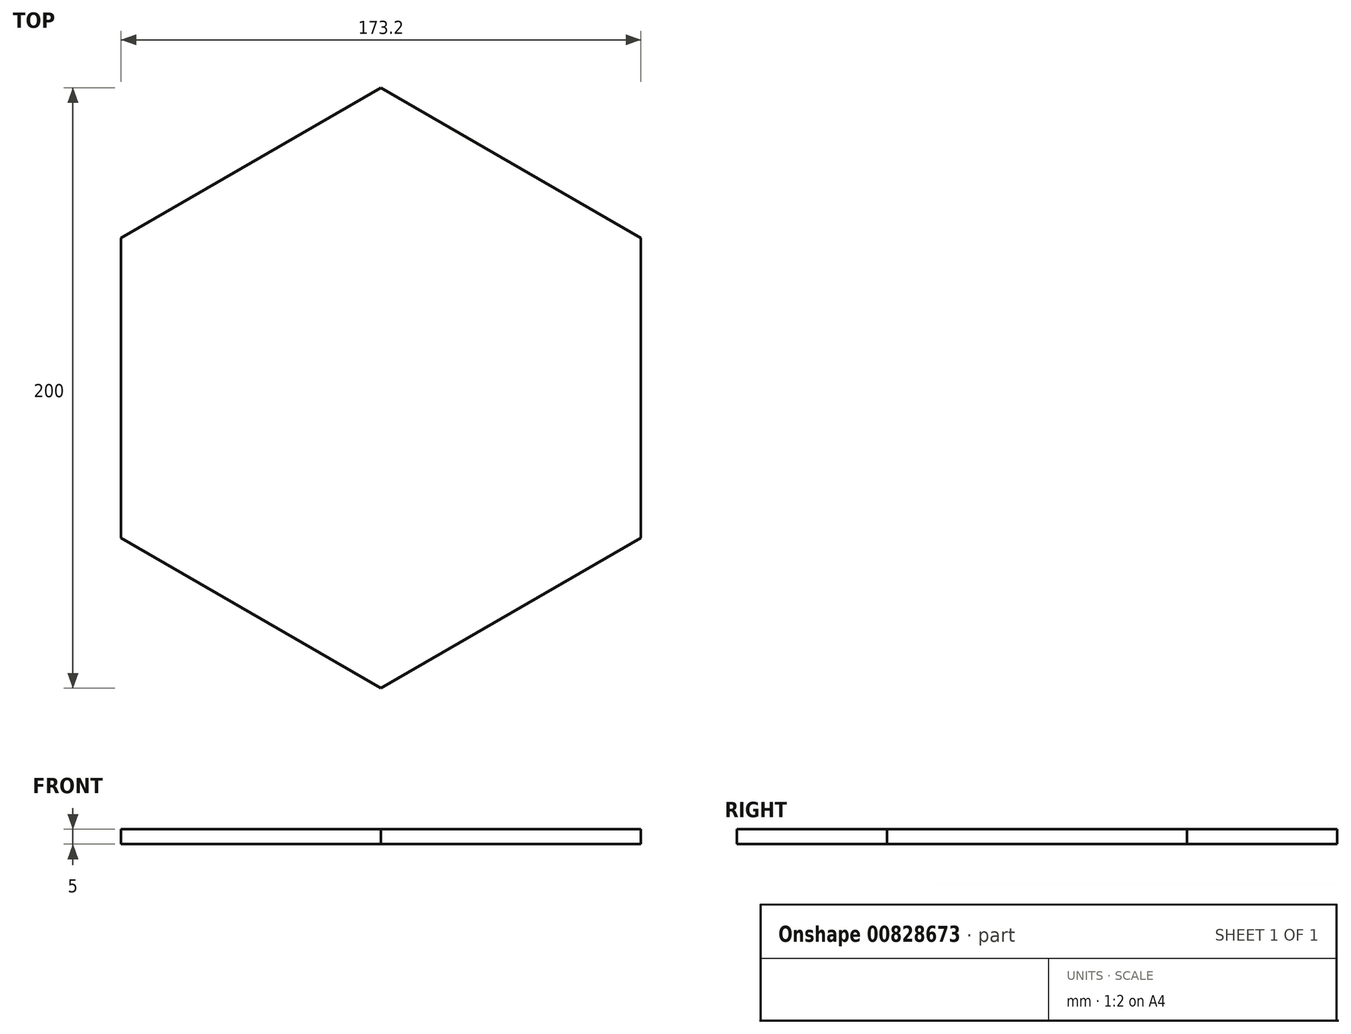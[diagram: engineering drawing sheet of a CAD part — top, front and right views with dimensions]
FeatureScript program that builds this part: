
annotation { "Feature Type Name" : "Feature", "Feature Type Description" : "" }
export const myFeature = defineFeature(function(context is Context, id is Id, definition is map)
    precondition{}
    {
        {
            var Q0;
            Q0=qCreatedBy(makeId("Top.planeOp"),FACE);
            var sketch = newSketch(context, id + "F0", { "sketchPlane" : qUnion([Q0])});
            skCircle(sketch, "E0.cCircle", {"center": v(0, 0) * mm, "radius": 86.6 * mm, "construction": true});
            skLineSegment(sketch, "E0.0", {"start": v(86.6, 50) * mm, "end": v(86.6, -50) * mm});
            skLineSegment(sketch, "E0.1", {"start": v(86.6, -50) * mm, "end": v(0, -100) * mm});
            skLineSegment(sketch, "E0.2", {"start": v(0, -100) * mm, "end": v(-86.6, -50) * mm});
            skLineSegment(sketch, "E0.3", {"start": v(-86.6, -50) * mm, "end": v(-86.6, 50) * mm});
            skLineSegment(sketch, "E0.4", {"start": v(-86.6, 50) * mm, "end": v(0, 100) * mm});
            skLineSegment(sketch, "E0.5", {"start": v(0, 100) * mm, "end": v(86.6, 50) * mm});
            skPoint(sketch, "E0.0.midPoint", {"position": v(86.6, 0) * mm});
            skSolve(sketch);
        }
        {
            var Q0;
            Q0 = qSketchRegion(id + "F0", true);
            extrude(context, id + "F1", {"entities" : qUnion([Q0]), "endBound" : BoundingType.SYMMETRIC, "depth" : 5 * mm, "offsetDistance" : 25 * mm});
        }
    });
